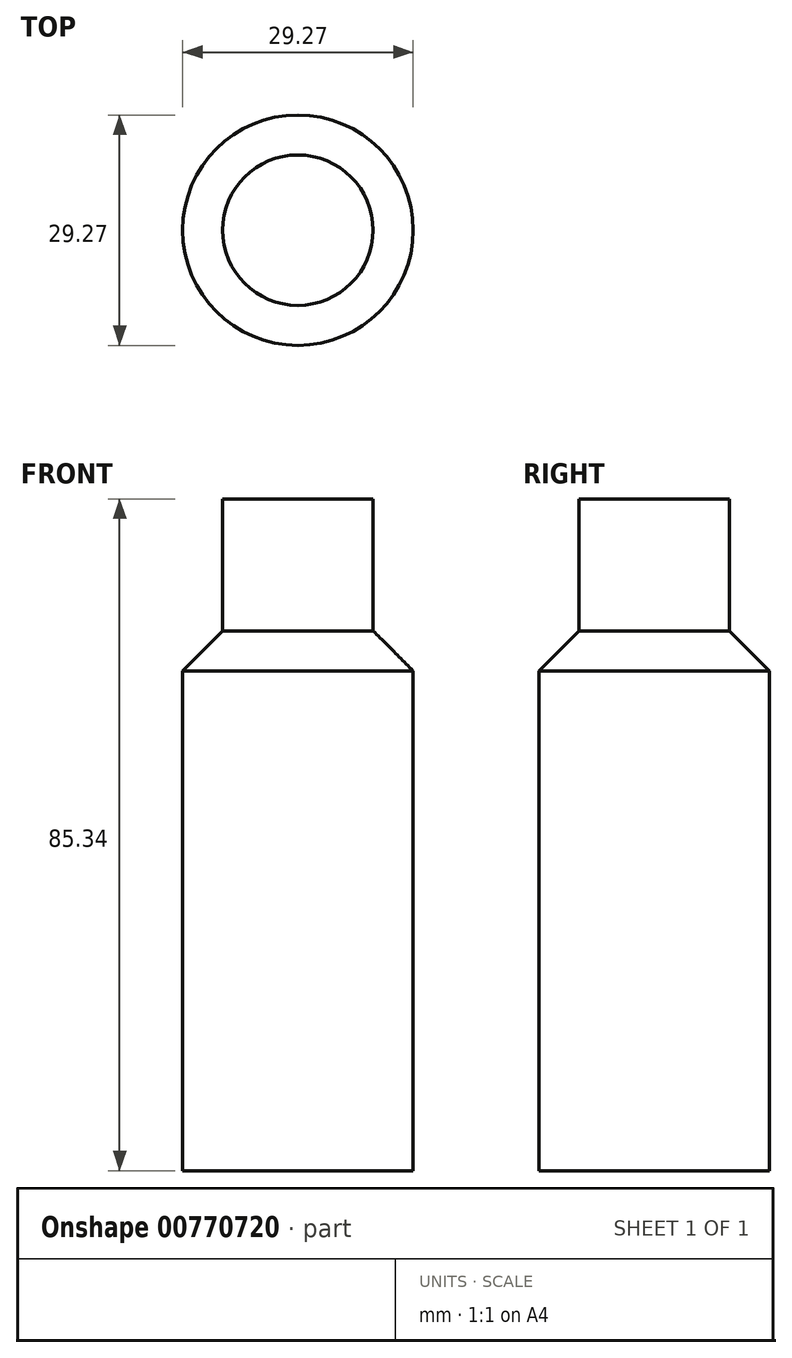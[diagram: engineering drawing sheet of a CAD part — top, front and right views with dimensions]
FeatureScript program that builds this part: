
annotation { "Feature Type Name" : "Feature", "Feature Type Description" : "" }
export const myFeature = defineFeature(function(context is Context, id is Id, definition is map)
    precondition{}
    {
        {
            var Q0;
            Q0=qCreatedBy(makeId("Top.planeOp"),FACE);
            var sketch = newSketch(context, id + "F0", { "sketchPlane" : qUnion([Q0])});
            skCircle(sketch, "E0", {"center": v(-54.8, 12.45) * mm, "radius": 14.64 * mm});
            skSolve(sketch);
        }
        {
            var Q0;
            Q0 = qSketchRegion(id + "F0", true);
            extrude(context, id + "F1", {"entities" : qUnion([Q0]), "depth" : 68.58 * mm, "offsetDistance" : 25.4 * mm});
        }
        {
            var Q0;
            Q0=makeQuery(id+"F1.opExtrude","CAP_EDGE",EDGE,{"disambiguationData":[OSD([sQuery(id+"F0.wireOp",EDGE,"E0")])],"isStart":false});
            chamfer(context, id + "F2", {"entities" : qUnion([Q0]), "width" : 5.08 * mm, "tangentPropagation" : true});
        }
        {
            var Q0;
            Q0=makeQuery(id+"F1.opExtrude","CAP_FACE",FACE,{"disambiguationData":[OSD([sQuery(id+"F0.wireOp",EDGE,"E0")])],"isStart":false});
            extrude(context, id + "F3", {"entities" : qUnion([Q0]), "operationType" : NewBodyOperationType.ADD, "depth" : 16.76 * mm, "offsetDistance" : 25.4 * mm});
        }
    });
